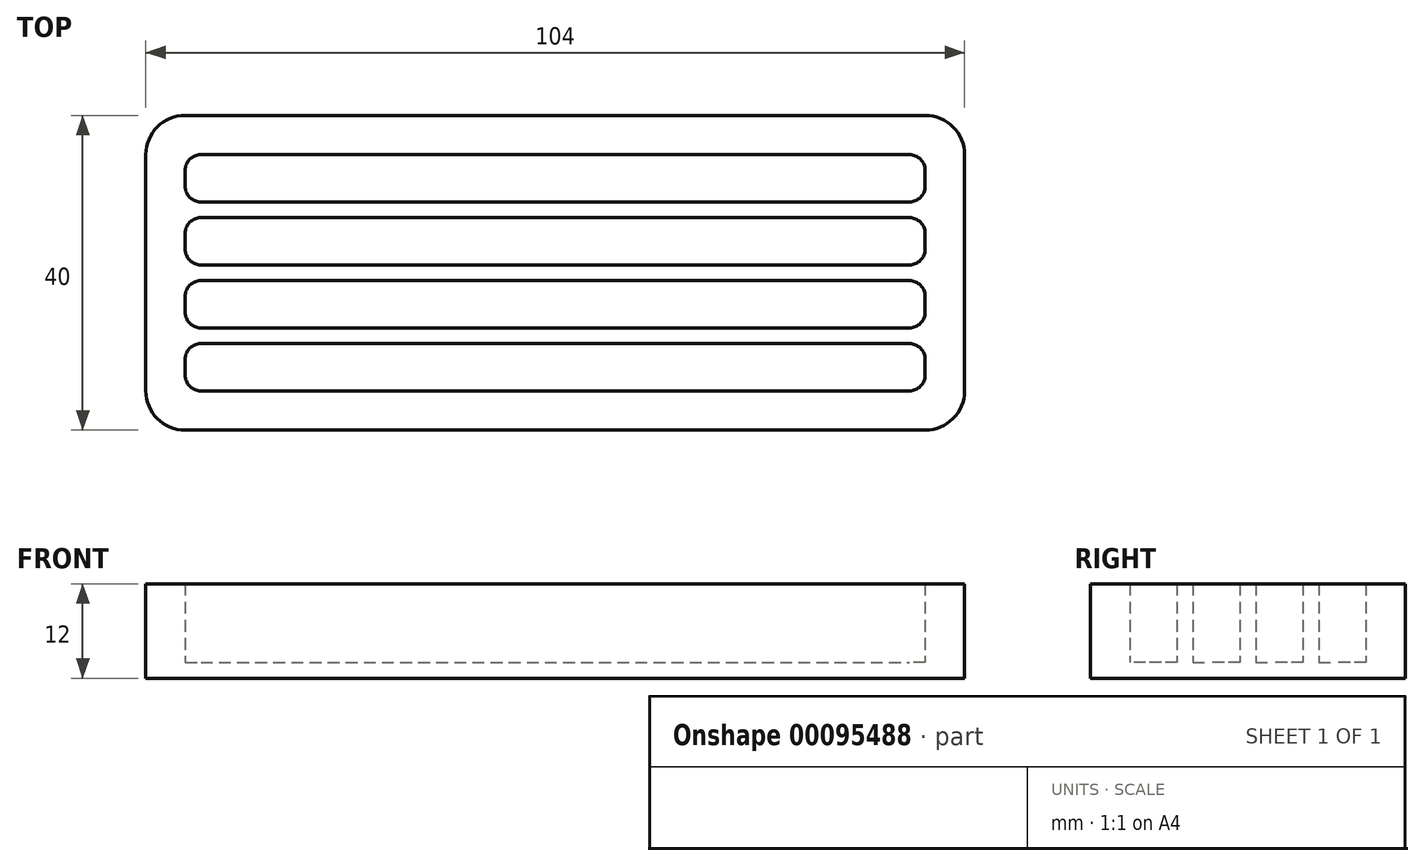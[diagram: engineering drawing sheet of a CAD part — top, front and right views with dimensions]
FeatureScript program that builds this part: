
annotation { "Feature Type Name" : "Feature", "Feature Type Description" : "" }
export const myFeature = defineFeature(function(context is Context, id is Id, definition is map)
    precondition{}
    {
        {
            var Q0;
            Q0=qCreatedBy(makeId("Top.planeOp"),FACE);
            var sketch = newSketch(context, id + "F0", { "sketchPlane" : qUnion([Q0])});
            skLineSegment(sketch, "E0.bottom", {"start": v(2, 6) * mm, "end": v(92, 6) * mm});
            skLineSegment(sketch, "E0.top", {"start": v(2, 0) * mm, "end": v(92, 0) * mm});
            skLineSegment(sketch, "E0.left", {"start": v(0, 4) * mm, "end": v(0, 2) * mm});
            skLineSegment(sketch, "E0.right", {"start": v(94, 4) * mm, "end": v(94, 2) * mm});
            skLineSegment(sketch, "E1.bottom", {"start": v(0, 35) * mm, "end": v(94, 35) * mm});
            skLineSegment(sketch, "E1.top", {"start": v(0, -5) * mm, "end": v(94, -5) * mm});
            skLineSegment(sketch, "E1.left", {"start": v(-5, 30) * mm, "end": v(-5, 0) * mm});
            skLineSegment(sketch, "E1.right", {"start": v(99, 30) * mm, "end": v(99, 0) * mm});
            skPoint(sketch, "E2.visualSharp", {"position": v(-5, 35) * mm});
            skArc(sketch, "E2.filletArc", {"start": v(0, 35) * mm, "mid": v(-3.54, 33.54) * mm, "end": v(-5, 30) * mm});
            skPoint(sketch, "E3.visualSharp", {"position": v(-5, -5) * mm});
            skArc(sketch, "E3.filletArc", {"start": v(-5, 0) * mm, "mid": v(-3.54, -3.54) * mm, "end": v(0, -5) * mm});
            skPoint(sketch, "E4.visualSharp", {"position": v(99, -5) * mm});
            skArc(sketch, "E4.filletArc", {"start": v(94, -5) * mm, "mid": v(97.54, -3.54) * mm, "end": v(99, 0) * mm});
            skPoint(sketch, "E5.visualSharp", {"position": v(99, 35) * mm});
            skArc(sketch, "E5.filletArc", {"start": v(99, 30) * mm, "mid": v(97.54, 33.54) * mm, "end": v(94, 35) * mm});
            skPoint(sketch, "E6.visualSharp", {"position": v(0, 6) * mm});
            skArc(sketch, "E6.filletArc", {"start": v(2, 6) * mm, "mid": v(0.59, 5.41) * mm, "end": v(0, 4) * mm});
            skArc(sketch, "E7.filletArc", {"start": v(0, 2) * mm, "mid": v(0.59, 0.59) * mm, "end": v(2, 0) * mm});
            skArc(sketch, "E8.filletArc", {"start": v(92, 0) * mm, "mid": v(93.41, 0.59) * mm, "end": v(94, 2) * mm});
            skPoint(sketch, "E9.visualSharp", {"position": v(94, 6) * mm});
            skArc(sketch, "E9.filletArc", {"start": v(94, 4) * mm, "mid": v(93.41, 5.41) * mm, "end": v(92, 6) * mm});
            skLineSegment(sketch, "E10.0.1.0", {"start": v(2, 14) * mm, "end": v(92, 14) * mm});
            skPoint(sketch, "E10.0.1.1", {"position": v(94, 14) * mm});
            skLineSegment(sketch, "E10.0.1.2", {"start": v(2, 8) * mm, "end": v(92, 8) * mm});
            skPoint(sketch, "E10.0.1.3", {"position": v(0, 14) * mm});
            skPoint(sketch, "E10.0.1.4", {"position": v(94, 8) * mm});
            skPoint(sketch, "E10.0.1.5", {"position": v(0, 8) * mm});
            skArc(sketch, "E10.0.1.6", {"start": v(94, 12) * mm, "mid": v(93.41, 13.41) * mm, "end": v(92, 14) * mm});
            skArc(sketch, "E10.0.1.7", {"start": v(2, 14) * mm, "mid": v(0.59, 13.41) * mm, "end": v(0, 12) * mm});
            skLineSegment(sketch, "E10.0.1.8", {"start": v(0, 12) * mm, "end": v(0, 10) * mm});
            skArc(sketch, "E10.0.1.9", {"start": v(92, 8) * mm, "mid": v(93.41, 8.59) * mm, "end": v(94, 10) * mm});
            skArc(sketch, "E10.0.1.10", {"start": v(0, 10) * mm, "mid": v(0.59, 8.59) * mm, "end": v(2, 8) * mm});
            skLineSegment(sketch, "E10.0.1.11", {"start": v(94, 12) * mm, "end": v(94, 10) * mm});
            skLineSegment(sketch, "E10.0.2.0", {"start": v(2, 22) * mm, "end": v(92, 22) * mm});
            skPoint(sketch, "E10.0.2.1", {"position": v(94, 22) * mm});
            skLineSegment(sketch, "E10.0.2.2", {"start": v(2, 16) * mm, "end": v(92, 16) * mm});
            skPoint(sketch, "E10.0.2.3", {"position": v(0, 22) * mm});
            skPoint(sketch, "E10.0.2.4", {"position": v(94, 16) * mm});
            skPoint(sketch, "E10.0.2.5", {"position": v(0, 16) * mm});
            skArc(sketch, "E10.0.2.6", {"start": v(94, 20) * mm, "mid": v(93.41, 21.41) * mm, "end": v(92, 22) * mm});
            skArc(sketch, "E10.0.2.7", {"start": v(2, 22) * mm, "mid": v(0.59, 21.41) * mm, "end": v(0, 20) * mm});
            skLineSegment(sketch, "E10.0.2.8", {"start": v(0, 20) * mm, "end": v(0, 18) * mm});
            skArc(sketch, "E10.0.2.9", {"start": v(92, 16) * mm, "mid": v(93.41, 16.59) * mm, "end": v(94, 18) * mm});
            skArc(sketch, "E10.0.2.10", {"start": v(0, 18) * mm, "mid": v(0.59, 16.59) * mm, "end": v(2, 16) * mm});
            skLineSegment(sketch, "E10.0.2.11", {"start": v(94, 20) * mm, "end": v(94, 18) * mm});
            skLineSegment(sketch, "E10.0.3.0", {"start": v(2, 30) * mm, "end": v(92, 30) * mm});
            skLineSegment(sketch, "E10.0.3.2", {"start": v(2, 24) * mm, "end": v(92, 24) * mm});
            skPoint(sketch, "E10.0.3.4", {"position": v(94, 24) * mm});
            skPoint(sketch, "E10.0.3.5", {"position": v(0, 24) * mm});
            skArc(sketch, "E10.0.3.6", {"start": v(94, 28) * mm, "mid": v(93.41, 29.41) * mm, "end": v(92, 30) * mm});
            skArc(sketch, "E10.0.3.7", {"start": v(2, 30) * mm, "mid": v(0.59, 29.41) * mm, "end": v(0, 28) * mm});
            skLineSegment(sketch, "E10.0.3.8", {"start": v(0, 28) * mm, "end": v(0, 26) * mm});
            skArc(sketch, "E10.0.3.9", {"start": v(92, 24) * mm, "mid": v(93.41, 24.59) * mm, "end": v(94, 26) * mm});
            skArc(sketch, "E10.0.3.10", {"start": v(0, 26) * mm, "mid": v(0.59, 24.59) * mm, "end": v(2, 24) * mm});
            skLineSegment(sketch, "E10.0.3.11", {"start": v(94, 28) * mm, "end": v(94, 26) * mm});
            skLineSegment(sketch, "E10.direction1", {"start": v(2, 6) * mm, "end": v(27, 6) * mm, "construction": true});
            skLineSegment(sketch, "E10.direction2", {"start": v(2, 6) * mm, "end": v(2, 14) * mm, "construction": true});
            skSolve(sketch);
        }
        {
            var Q0;
            Q0=makeQuery(id+"F0.imprint","IMPRINT",FACE,{"disambiguationData":[TD([[makeQuery(id+"F0.imprint","IMPRINT",EDGE,{"derivedFrom":sQuery(id+"F0.wireOp",EDGE,"E0.bottom")}),1.0]])]});
            extrude(context, id + "F1", {"entities" : qUnion([Q0]), "depth" : 10 * mm});
        }
        {
            var Q0;
            Q0=makeQuery(id+"F0.imprint","IMPRINT",FACE,{"disambiguationData":[TD([[makeQuery(id+"F0.imprint","IMPRINT",EDGE,{"derivedFrom":sQuery(id+"F0.wireOp",EDGE,"E0.bottom")}),1.0]])]});
            var Q1;
            Q1=makeQuery(id+"F0.imprint","IMPRINT",FACE,{"disambiguationData":[TD([[makeQuery(id+"F0.imprint","IMPRINT",EDGE,{"derivedFrom":sQuery(id+"F0.wireOp",EDGE,"E0.bottom")}),-1.0]])]});
            var Q2;
            Q2=makeQuery(id+"F0.imprint","IMPRINT",FACE,{"disambiguationData":[TD([[makeQuery(id+"F0.imprint","IMPRINT",EDGE,{"derivedFrom":sQuery(id+"F0.wireOp",EDGE,"E10.0.1.0")}),-1.0]])]});
            var Q3;
            Q3=makeQuery(id+"F0.imprint","IMPRINT",FACE,{"disambiguationData":[TD([[makeQuery(id+"F0.imprint","IMPRINT",EDGE,{"derivedFrom":sQuery(id+"F0.wireOp",EDGE,"E10.0.2.0")}),-1.0]])]});
            var Q4;
            Q4=makeQuery(id+"F0.imprint","IMPRINT",FACE,{"disambiguationData":[TD([[makeQuery(id+"F0.imprint","IMPRINT",EDGE,{"derivedFrom":sQuery(id+"F0.wireOp",EDGE,"E10.0.3.0")}),-1.0]])]});
            extrude(context, id + "F2", {"entities" : qUnion([Q0, Q1, Q2, Q3, Q4]), "operationType" : NewBodyOperationType.ADD, "oppositeDirection" : true, "depth" : 2 * mm});
        }
    });
